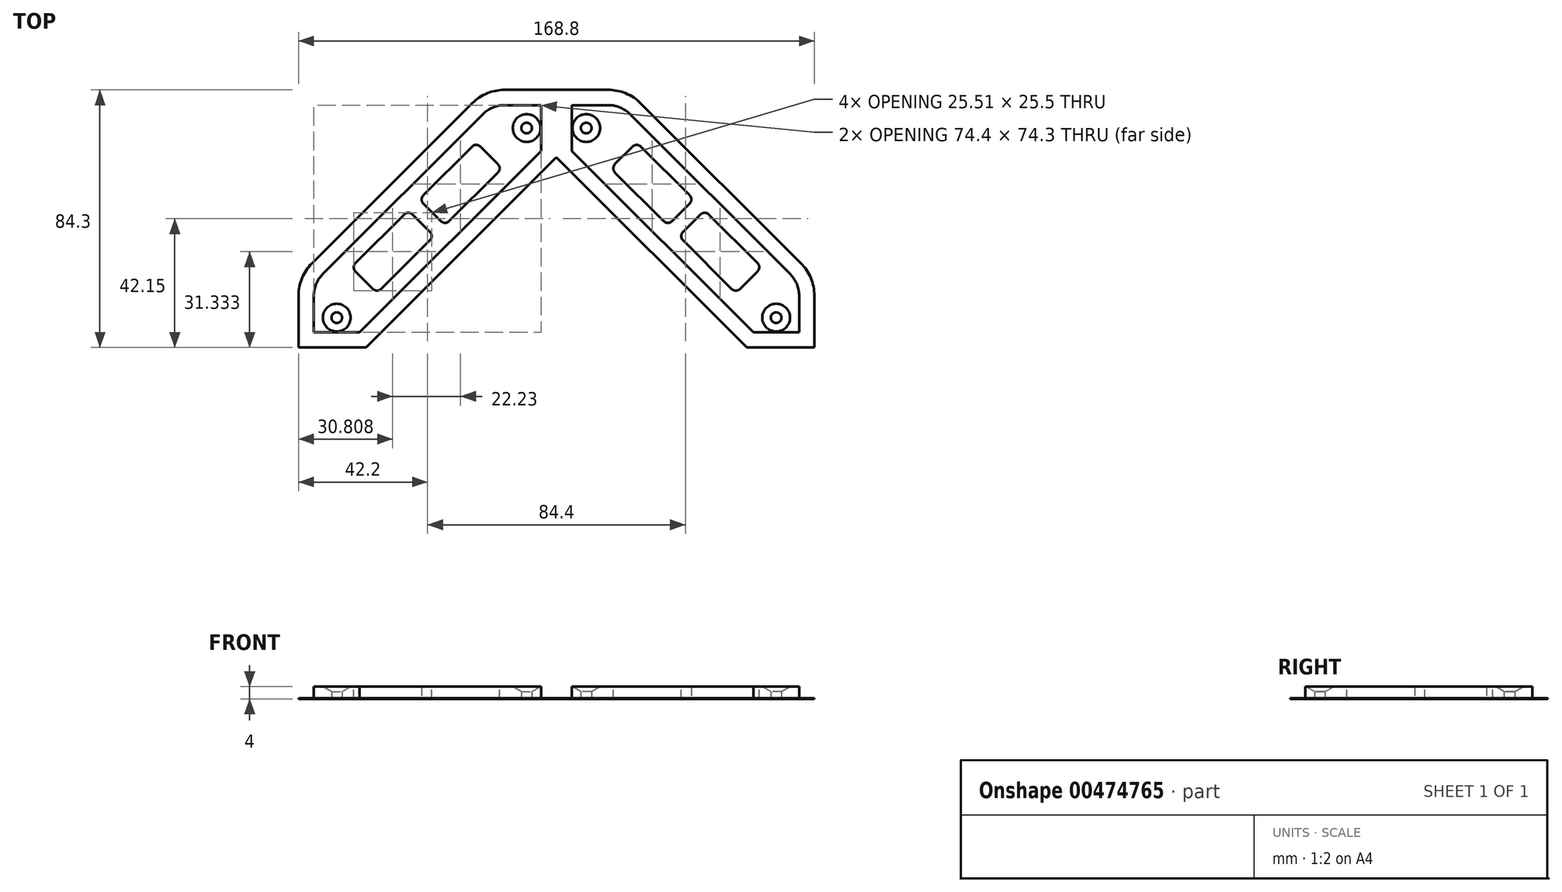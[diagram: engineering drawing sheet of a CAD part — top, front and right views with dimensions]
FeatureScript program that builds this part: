
annotation { "Feature Type Name" : "Feature", "Feature Type Description" : "" }
export const myFeature = defineFeature(function(context is Context, id is Id, definition is map)
    precondition{}
    {
        {
            var Q0;
            Q0=qCreatedBy(makeId("Top.planeOp"),FACE);
            var sketch = newSketch(context, id + "F0", { "sketchPlane" : qUnion([Q0])});
            skLineSegment(sketch, "E0.bottom", {"start": v(0, 0) * mm, "end": v(9.5, 0) * mm, "construction": true});
            skLineSegment(sketch, "E0.top", {"start": v(0, -15) * mm, "end": v(9.5, -15) * mm, "construction": true});
            skLineSegment(sketch, "E0.left", {"start": v(0, 0) * mm, "end": v(0, -15) * mm});
            skLineSegment(sketch, "E0.right", {"start": v(9.5, 0) * mm, "end": v(9.5, -15) * mm, "construction": true});
            skLineSegment(sketch, "E1.bottom", {"start": v(59.4, -64.8) * mm, "end": v(74.4, -64.8) * mm, "construction": true});
            skLineSegment(sketch, "E1.top", {"start": v(59.4, -74.3) * mm, "end": v(74.4, -74.3) * mm});
            skLineSegment(sketch, "E1.left", {"start": v(59.4, -64.8) * mm, "end": v(59.4, -74.3) * mm, "construction": true});
            skLineSegment(sketch, "E1.right", {"start": v(74.4, -64.8) * mm, "end": v(74.4, -74.3) * mm, "construction": true});
            skCircle(sketch, "E2", {"center": v(4.75, -7.5) * mm, "radius": 1.75 * mm});
            skCircle(sketch, "E3", {"center": v(66.9, -69.55) * mm, "radius": 1.75 * mm});
            skLineSegment(sketch, "E4", {"start": v(0, -15) * mm, "end": v(59.4, -74.3) * mm});
            skLineSegment(sketch, "E5", {"start": v(0, 0) * mm, "end": v(16.11, 0) * mm});
            skLineSegment(sketch, "E6", {"start": v(16.11, 0) * mm, "end": v(74.4, -58.19) * mm});
            skLineSegment(sketch, "E7", {"start": v(74.4, -58.19) * mm, "end": v(74.4, -74.3) * mm});
            skLineSegment(sketch, "E8", {"start": v(12.78, -20.7) * mm, "end": v(21.26, -12.2) * mm});
            skLineSegment(sketch, "E9", {"start": v(21.26, -12.2) * mm, "end": v(39.95, -30.86) * mm});
            skLineSegment(sketch, "E10", {"start": v(62.18, -53.05) * mm, "end": v(53.7, -61.54) * mm});
            skLineSegment(sketch, "E11", {"start": v(53.7, -61.54) * mm, "end": v(35, -42.88) * mm});
            skLineSegment(sketch, "E12", {"start": v(33.24, -41.12) * mm, "end": v(41.72, -32.62) * mm, "construction": true});
            skLineSegment(sketch, "E13", {"start": v(31.47, -39.35) * mm, "end": v(39.95, -30.86) * mm});
            skLineSegment(sketch, "E14", {"start": v(35, -42.88) * mm, "end": v(43.49, -34.4) * mm});
            skLineSegment(sketch, "E15.trimOffspring", {"start": v(43.49, -34.4) * mm, "end": v(62.18, -53.05) * mm});
            skLineSegment(sketch, "E16.trimOffspring", {"start": v(31.47, -39.35) * mm, "end": v(12.78, -20.7) * mm});
            skSolve(sketch);
        }
        {
            var Q0;
            Q0=qSketchRegion(id+"F0",true);
            extrude(context, id + "F1", {"entities" : qUnion([Q0]), "depth" : 4 * mm, "offsetDistance" : 25 * mm});
        }
        {
            var Q0;
            Q0=makeQuery(id+"F1.opExtrude","SWEPT_EDGE",EDGE,{"disambiguationData":[OSD([sQuery(id+"F0.wireOp",EDGE,"E5"),sQuery(id+"F0.wireOp",EDGE,"E6")])]});
            var Q1;
            Q1=makeQuery(id+"F1.opExtrude","SWEPT_EDGE",EDGE,{"disambiguationData":[OSD([sQuery(id+"F0.wireOp",EDGE,"E6"),sQuery(id+"F0.wireOp",EDGE,"E7")])]});
            fillet(context, id + "F2", {"entities" : qUnion([Q0, Q1]), "radius" : 10 * mm, "tangentPropagation" : true, "allowEdgeOverflow" : false});
        }
        {
            var Q0;
            Q0=makeQuery(id+"F1.opExtrude","SWEPT_EDGE",EDGE,{"disambiguationData":[OSD([sQuery(id+"F0.wireOp",EDGE,"E8"),sQuery(id+"F0.wireOp",EDGE,"E9")])]});
            var Q1;
            Q1=makeQuery(id+"F1.opExtrude","SWEPT_EDGE",EDGE,{"disambiguationData":[OSD([sQuery(id+"F0.wireOp",EDGE,"E8"),sQuery(id+"F0.wireOp",EDGE,"E16.trimOffspring")])]});
            var Q2;
            Q2=makeQuery(id+"F1.opExtrude","SWEPT_EDGE",EDGE,{"disambiguationData":[OSD([sQuery(id+"F0.wireOp",EDGE,"E9"),sQuery(id+"F0.wireOp",EDGE,"E13")])]});
            var Q3;
            Q3=makeQuery(id+"F1.opExtrude","SWEPT_EDGE",EDGE,{"disambiguationData":[OSD([sQuery(id+"F0.wireOp",EDGE,"E13"),sQuery(id+"F0.wireOp",EDGE,"E16.trimOffspring")])]});
            var Q4;
            Q4=makeQuery(id+"F1.opExtrude","SWEPT_EDGE",EDGE,{"disambiguationData":[OSD([sQuery(id+"F0.wireOp",EDGE,"E10"),sQuery(id+"F0.wireOp",EDGE,"E11")])]});
            var Q5;
            Q5=makeQuery(id+"F1.opExtrude","SWEPT_EDGE",EDGE,{"disambiguationData":[OSD([sQuery(id+"F0.wireOp",EDGE,"E10"),sQuery(id+"F0.wireOp",EDGE,"E15.trimOffspring")])]});
            var Q6;
            Q6=makeQuery(id+"F1.opExtrude","SWEPT_EDGE",EDGE,{"disambiguationData":[OSD([sQuery(id+"F0.wireOp",EDGE,"E14"),sQuery(id+"F0.wireOp",EDGE,"E15.trimOffspring")])]});
            var Q7;
            Q7=makeQuery(id+"F1.opExtrude","SWEPT_EDGE",EDGE,{"disambiguationData":[OSD([sQuery(id+"F0.wireOp",EDGE,"E11"),sQuery(id+"F0.wireOp",EDGE,"E14")])]});
            fillet(context, id + "F3", {"entities" : qUnion([Q0, Q1, Q2, Q3, Q4, Q5, Q6, Q7]), "radius" : 2 * mm, "tangentPropagation" : true, "allowEdgeOverflow" : false});
        }
        {
            var Q0;
            Q0=makeQuery(id+"F1.opExtrude","CAP_EDGE",EDGE,{"disambiguationData":[OSD([sQuery(id+"F0.wireOp",EDGE,"E2")])],"isStart":false});
            var Q1;
            Q1=makeQuery(id+"F1.opExtrude","CAP_EDGE",EDGE,{"disambiguationData":[OSD([sQuery(id+"F0.wireOp",EDGE,"E3")])],"isStart":false});
            chamfer(context, id + "F4", {"entities" : qUnion([Q0, Q1]), "chamferType" : ChamferType.TWO_OFFSETS, "width1" : 2.8 * mm, "oppositeDirection" : false, "width2" : 1.6 * mm, "tangentPropagation" : true});
        }
        {
            var Q0;
            Q0=qCreatedBy(makeId("Right.planeOp"),FACE);
            cPlane(context, id + "F5", {"entities" : qUnion([Q0]), "cplaneType" : CPlaneType.OFFSET, "offset" : 5 * mm, "oppositeDirection" : true, "width" : 150 * mm, "height" : 150 * mm});
        }
        {
            var Q0;
            Q0=makeQuery(id+"F1.opExtrude","SWEPT_BODY",BODY,{"disambiguationData":[OSD([sQuery(id+"F0.wireOp",EDGE,"E0.left"),sQuery(id+"F0.wireOp",EDGE,"E1.top"),sQuery(id+"F0.wireOp",EDGE,"E2"),sQuery(id+"F0.wireOp",EDGE,"E3"),sQuery(id+"F0.wireOp",EDGE,"E4"),sQuery(id+"F0.wireOp",EDGE,"E5"),sQuery(id+"F0.wireOp",EDGE,"E6"),sQuery(id+"F0.wireOp",EDGE,"E7"),sQuery(id+"F0.wireOp",EDGE,"E8"),sQuery(id+"F0.wireOp",EDGE,"E9"),sQuery(id+"F0.wireOp",EDGE,"E10"),sQuery(id+"F0.wireOp",EDGE,"E11"),sQuery(id+"F0.wireOp",EDGE,"E13"),sQuery(id+"F0.wireOp",EDGE,"E14"),sQuery(id+"F0.wireOp",EDGE,"E15.trimOffspring"),sQuery(id+"F0.wireOp",EDGE,"E16.trimOffspring")])]});
            var Q1;
            Q1=qCreatedBy(id+"F5.planeOp",FACE);
            mirror(context, id + "F6", {"entities" : qUnion([Q0]), "mirrorPlane" : qUnion([Q1])});
        }
        {
            var Q0;
            Q0=qCreatedBy(makeId("Top.planeOp"),FACE);
            var sketch = newSketch(context, id + "F7", { "sketchPlane" : qUnion([Q0])});
            skLineSegment(sketch, "E17", {"start": v(-85, -51.72) * mm, "end": v(-32.57, 0.62) * mm});
            skLineSegment(sketch, "E18", {"start": v(-21.98, 5) * mm, "end": v(11.98, 5) * mm});
            skLineSegment(sketch, "E19", {"start": v(22.57, 0.62) * mm, "end": v(75, -51.72) * mm});
            skLineSegment(sketch, "E20", {"start": v(79.4, -62.34) * mm, "end": v(79.4, -79.3) * mm});
            skLineSegment(sketch, "E21", {"start": v(79.4, -79.3) * mm, "end": v(57.33, -79.3) * mm});
            skLineSegment(sketch, "E22", {"start": v(57.33, -79.3) * mm, "end": v(-5, -17.07) * mm});
            skLineSegment(sketch, "E23", {"start": v(-5, -17.07) * mm, "end": v(-67.33, -79.3) * mm});
            skLineSegment(sketch, "E24", {"start": v(-67.33, -79.3) * mm, "end": v(-89.4, -79.3) * mm});
            skLineSegment(sketch, "E25", {"start": v(-89.4, -79.3) * mm, "end": v(-89.4, -62.34) * mm});
            skArc(sketch, "E26", {"start": v(-21.98, 5) * mm, "mid": v(-27.71, 3.86) * mm, "end": v(-32.57, 0.62) * mm});
            skArc(sketch, "E27", {"start": v(22.57, 0.62) * mm, "mid": v(17.71, 3.86) * mm, "end": v(11.98, 5) * mm});
            skArc(sketch, "E28", {"start": v(-85, -51.72) * mm, "mid": v(-88.26, -56.59) * mm, "end": v(-89.4, -62.34) * mm});
            skArc(sketch, "E29", {"start": v(79.4, -62.34) * mm, "mid": v(78.26, -56.59) * mm, "end": v(75, -51.72) * mm});
            skLineSegment(sketch, "E30", {"start": v(-84.4, -74.3) * mm, "end": v(-69.4, -74.3) * mm});
            skLineSegment(sketch, "E31", {"start": v(-69.4, -74.3) * mm, "end": v(-10, -15) * mm});
            skLineSegment(sketch, "E32", {"start": v(-10, -15) * mm, "end": v(-10, 0) * mm});
            skLineSegment(sketch, "E33", {"start": v(-84.4, -74.3) * mm, "end": v(-84.4, -62.34) * mm});
            skArc(sketch, "E34", {"start": v(-81.47, -55.26) * mm, "mid": v(-83.64, -58.5) * mm, "end": v(-84.4, -62.34) * mm});
            skLineSegment(sketch, "E35", {"start": v(-81.47, -55.26) * mm, "end": v(-29.04, -2.92) * mm});
            skArc(sketch, "E36", {"start": v(-21.98, 0) * mm, "mid": v(-25.8, -0.76) * mm, "end": v(-29.04, -2.92) * mm});
            skLineSegment(sketch, "E37", {"start": v(-21.98, 0) * mm, "end": v(-10, 0) * mm});
            skLineSegment(sketch, "E38", {"start": v(0, 0) * mm, "end": v(0, -15) * mm});
            skLineSegment(sketch, "E39", {"start": v(0, -15) * mm, "end": v(59.4, -74.3) * mm});
            skLineSegment(sketch, "E40", {"start": v(59.4, -74.3) * mm, "end": v(74.4, -74.3) * mm});
            skLineSegment(sketch, "E41", {"start": v(0, 0) * mm, "end": v(11.98, 0) * mm});
            skLineSegment(sketch, "E42", {"start": v(74.4, -74.3) * mm, "end": v(74.4, -62.34) * mm});
            skLineSegment(sketch, "E43", {"start": v(19.04, -2.92) * mm, "end": v(71.47, -55.26) * mm});
            skArc(sketch, "E44", {"start": v(19.04, -2.92) * mm, "mid": v(15.8, -0.76) * mm, "end": v(11.98, 0) * mm});
            skArc(sketch, "E45", {"start": v(74.4, -62.34) * mm, "mid": v(73.64, -58.5) * mm, "end": v(71.47, -55.26) * mm});
            skSolve(sketch);
        }
        {
            var Q0;
            Q0 = qSketchRegion(id + "F7", true);
            extrude(context, id + "F8", {"entities" : qUnion([Q0]), "depth" : 0.2 * mm, "offsetDistance" : 25 * mm});
        }
    });
